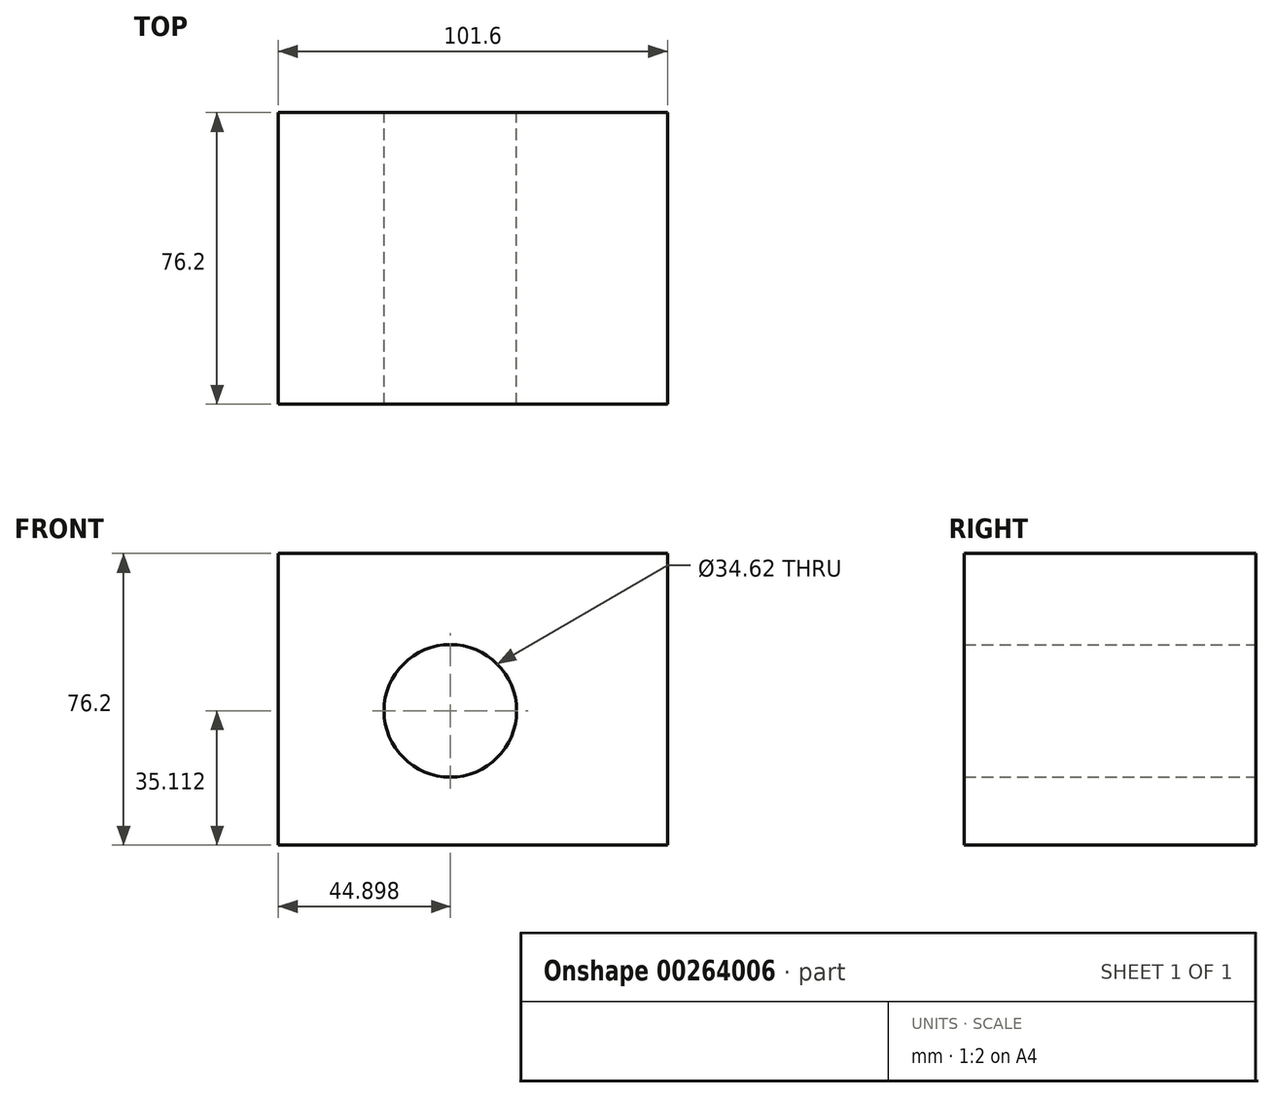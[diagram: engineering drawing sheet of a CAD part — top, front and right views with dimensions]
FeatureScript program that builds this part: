
annotation { "Feature Type Name" : "Feature", "Feature Type Description" : "" }
export const myFeature = defineFeature(function(context is Context, id is Id, definition is map)
    precondition{}
    {
        {
            var Q0;
            Q0=qCreatedBy(makeId("Front.planeOp"),FACE);
            var sketch = newSketch(context, id + "F0", { "sketchPlane" : qUnion([Q0])});
            skLineSegment(sketch, "E0.bottom", {"start": v(0, 0) * mm, "end": v(101.6, 0) * mm});
            skLineSegment(sketch, "E0.top", {"start": v(0, 76.2) * mm, "end": v(101.6, 76.2) * mm});
            skLineSegment(sketch, "E0.left", {"start": v(0, 0) * mm, "end": v(0, 76.2) * mm});
            skLineSegment(sketch, "E0.right", {"start": v(101.6, 0) * mm, "end": v(101.6, 76.2) * mm});
            skSolve(sketch);
        }
        {
            var Q0;
            Q0=makeQuery(id+"F0.imprint","IMPRINT",FACE,{"disambiguationData":[TD([[makeQuery(id+"F0.imprint","IMPRINT",EDGE,{"derivedFrom":sQuery(id+"F0.wireOp",EDGE,"E0.bottom")}),1.0]])]});
            extrude(context, id + "F1", {"entities" : qUnion([Q0]), "depth" : 76.2 * mm});
        }
        {
            var Q0;
            Q0=qCreatedBy(makeId("Front.planeOp"),FACE);
            var sketch = newSketch(context, id + "F2", { "sketchPlane" : qUnion([Q0])});
            skCircle(sketch, "E1", {"center": v(44.9, 35.11) * mm, "radius": 17.3 * mm});
            skSolve(sketch);
        }
        {
            var Q0;
            Q0=makeQuery(id+"F2.imprint","IMPRINT",FACE,{"disambiguationData":[TD([[makeQuery(id+"F2.imprint","IMPRINT",EDGE,{"derivedFrom":sQuery(id+"F2.wireOp",EDGE,"E1")}),1.0]])]});
            extrude(context, id + "F3", {"entities" : qUnion([Q0]), "operationType" : NewBodyOperationType.REMOVE, "endBound" : BoundingType.UP_TO_NEXT, "depth" : 25.4 * mm});
        }
    });
